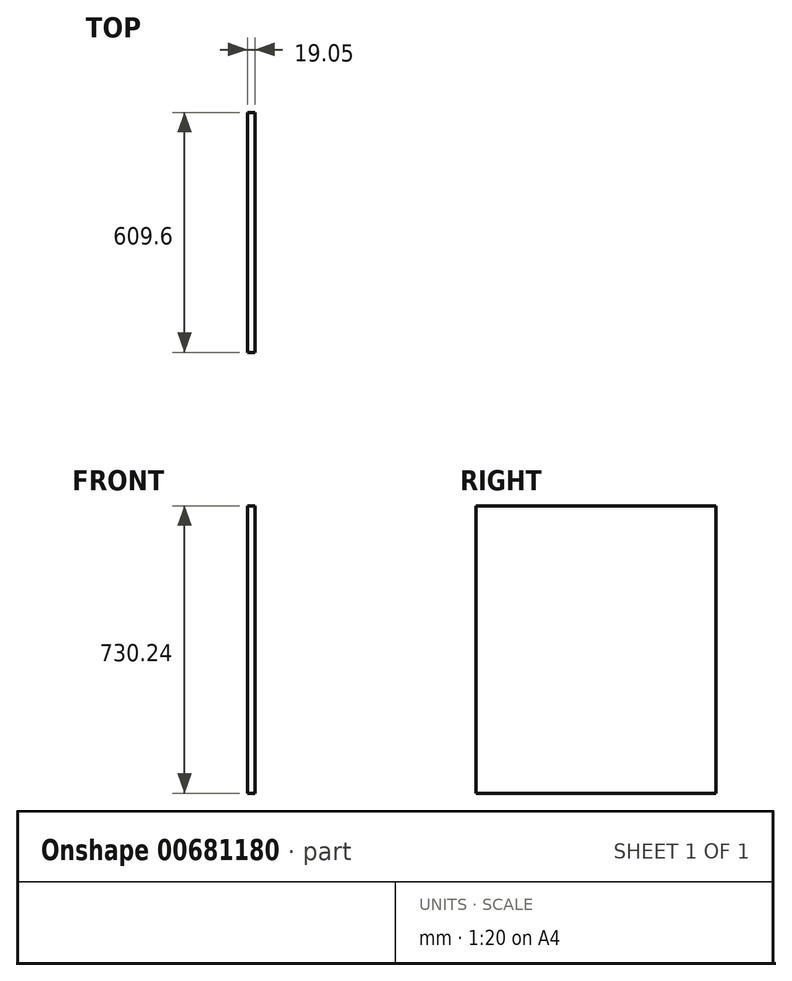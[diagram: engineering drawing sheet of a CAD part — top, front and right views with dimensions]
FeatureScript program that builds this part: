
annotation { "Feature Type Name" : "Feature", "Feature Type Description" : "" }
export const myFeature = defineFeature(function(context is Context, id is Id, definition is map)
    precondition{}
    {
        {
            var Q0;
            Q0=qCreatedBy(makeId("Right.planeOp"),FACE);
            var sketch = newSketch(context, id + "F0", { "sketchPlane" : qUnion([Q0])});
            skLineSegment(sketch, "E0.bottom", {"start": v(304.8, 365.13) * mm, "end": v(-304.8, 365.13) * mm});
            skLineSegment(sketch, "E0.top", {"start": v(304.8, -365.13) * mm, "end": v(-304.8, -365.13) * mm});
            skLineSegment(sketch, "E0.left", {"start": v(304.8, 365.12) * mm, "end": v(304.8, -365.13) * mm});
            skLineSegment(sketch, "E0.right", {"start": v(-304.8, 365.13) * mm, "end": v(-304.8, -365.13) * mm});
            skPoint(sketch, "E0.middle", {"position": v(0, 0) * mm});
            skSolve(sketch);
        }
        {
            var Q0;
            Q0=makeQuery(id+"F0.imprint","IMPRINT",FACE,{"disambiguationData":[TD([[makeQuery(id+"F0.imprint","IMPRINT",EDGE,{"derivedFrom":sQuery(id+"F0.wireOp",EDGE,"E0.bottom")}),1.0]])]});
            extrude(context, id + "F1", {"entities" : qUnion([Q0]), "depth" : 19.05 * mm, "offsetDistance" : 25.4 * mm});
        }
    });
